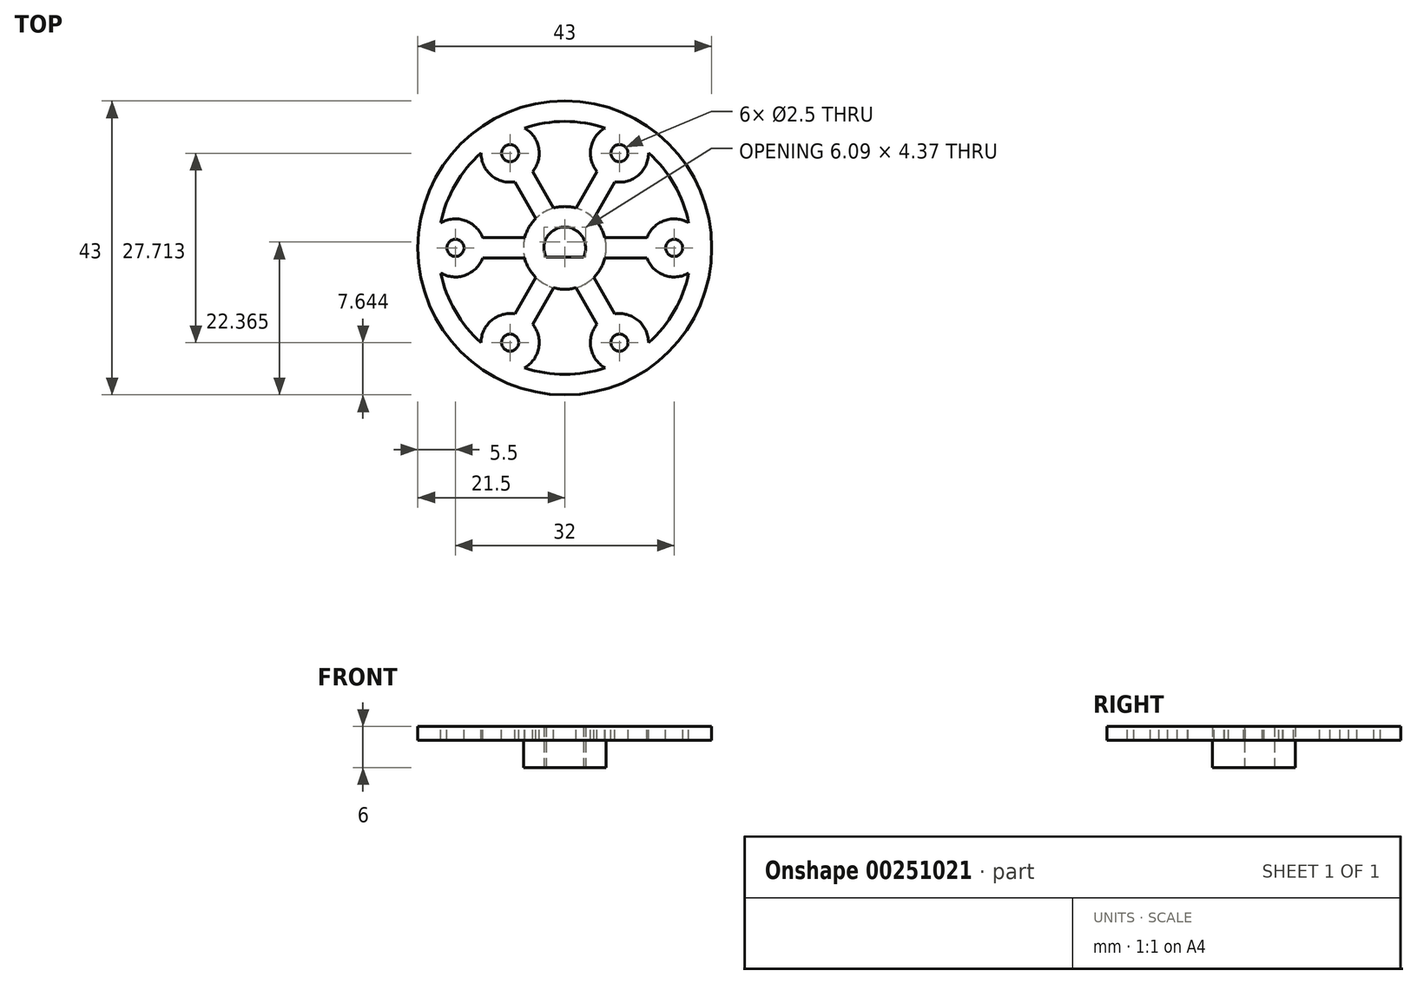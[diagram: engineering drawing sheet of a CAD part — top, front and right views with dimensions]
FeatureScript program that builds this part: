
annotation { "Feature Type Name" : "Feature", "Feature Type Description" : "" }
export const myFeature = defineFeature(function(context is Context, id is Id, definition is map)
    precondition{}
    {
        {
            var Q0;
            Q0=qCreatedBy(makeId("Top.planeOp"),FACE);
            var sketch = newSketch(context, id + "F0", { "sketchPlane" : qUnion([Q0])});
            skCircle(sketch, "E0", {"center": v(0, 0) * mm, "radius": 3.05 * mm, "construction": true});
            skLineSegment(sketch, "E1", {"start": v(-2.75, -1.32) * mm, "end": v(2.75, -1.32) * mm});
            skArc(sketch, "E2", {"start": v(2.75, -1.32) * mm, "mid": v(0, 3.05) * mm, "end": v(-2.75, -1.32) * mm});
            skCircle(sketch, "E3", {"center": v(0, 0) * mm, "radius": 6.05 * mm});
            skSolve(sketch);
        }
        {
            var Q0;
            Q0 = qSketchRegion(id + "F0", true);
            extrude(context, id + "F1", {"entities" : qUnion([Q0]), "depth" : 6 * mm});
        }
        {
            var Q0;
            Q0=makeQuery(id+"F1.opExtrude","CAP_FACE",FACE,{"disambiguationData":[OSD([sQuery(id+"F0.wireOp",EDGE,"E1"),sQuery(id+"F0.wireOp",EDGE,"E2"),sQuery(id+"F0.wireOp",EDGE,"E3")])],"isStart":false});
            var sketch = newSketch(context, id + "F2", { "sketchPlane" : qUnion([Q0])});
            skCircle(sketch, "E4", {"center": v(0, 0) * mm, "radius": 21.5 * mm});
            skCircle(sketch, "E5", {"center": v(0, 0) * mm, "radius": 18.5 * mm});
            skCircle(sketch, "E6", {"center": v(-16, 0) * mm, "radius": 1.25 * mm});
            skCircle(sketch, "E7", {"center": v(-16, 0) * mm, "radius": 4.25 * mm});
            skCircle(sketch, "E8.1.0", {"center": v(-8, -13.86) * mm, "radius": 1.25 * mm});
            skCircle(sketch, "E8.1.1", {"center": v(-8, -13.86) * mm, "radius": 4.25 * mm});
            skCircle(sketch, "E8.2.0", {"center": v(8, -13.86) * mm, "radius": 1.25 * mm});
            skCircle(sketch, "E8.2.1", {"center": v(8, -13.86) * mm, "radius": 4.25 * mm});
            skCircle(sketch, "E8.3.0", {"center": v(16, 0) * mm, "radius": 1.25 * mm});
            skCircle(sketch, "E8.3.1", {"center": v(16, 0) * mm, "radius": 4.25 * mm});
            skCircle(sketch, "E8.4.0", {"center": v(8, 13.86) * mm, "radius": 1.25 * mm});
            skCircle(sketch, "E8.4.1", {"center": v(8, 13.86) * mm, "radius": 4.25 * mm});
            skCircle(sketch, "E8.5.0", {"center": v(-8, 13.86) * mm, "radius": 1.25 * mm});
            skCircle(sketch, "E8.5.1", {"center": v(-8, 13.86) * mm, "radius": 4.25 * mm});
            skLineSegment(sketch, "E9.bottom", {"start": v(-4, 1.5) * mm, "end": v(-14, 1.5) * mm});
            skLineSegment(sketch, "E9.top", {"start": v(-4, -1.5) * mm, "end": v(-14, -1.5) * mm});
            skLineSegment(sketch, "E9.left", {"start": v(-4, 1.5) * mm, "end": v(-4, -1.5) * mm});
            skLineSegment(sketch, "E9.right", {"start": v(-14, 1.5) * mm, "end": v(-14, -1.5) * mm});
            skPoint(sketch, "E9.middle", {"position": v(-9, 0) * mm});
            skLineSegment(sketch, "E10.1.0", {"start": v(-3.3, -2.71) * mm, "end": v(-8.3, -11.37) * mm});
            skLineSegment(sketch, "E10.1.1", {"start": v(-8.3, -11.37) * mm, "end": v(-5.7, -12.87) * mm});
            skLineSegment(sketch, "E10.1.2", {"start": v(-0.7, -4.21) * mm, "end": v(-5.7, -12.87) * mm});
            skLineSegment(sketch, "E10.1.3", {"start": v(-3.3, -2.71) * mm, "end": v(-0.7, -4.21) * mm});
            skLineSegment(sketch, "E10.2.0", {"start": v(0.7, -4.21) * mm, "end": v(5.7, -12.87) * mm});
            skLineSegment(sketch, "E10.2.1", {"start": v(5.7, -12.87) * mm, "end": v(8.3, -11.37) * mm});
            skLineSegment(sketch, "E10.2.2", {"start": v(3.3, -2.71) * mm, "end": v(8.3, -11.37) * mm});
            skLineSegment(sketch, "E10.2.3", {"start": v(0.7, -4.21) * mm, "end": v(3.3, -2.71) * mm});
            skLineSegment(sketch, "E10.3.0", {"start": v(4, -1.5) * mm, "end": v(14, -1.5) * mm});
            skLineSegment(sketch, "E10.3.1", {"start": v(14, -1.5) * mm, "end": v(14, 1.5) * mm});
            skLineSegment(sketch, "E10.3.2", {"start": v(4, 1.5) * mm, "end": v(14, 1.5) * mm});
            skLineSegment(sketch, "E10.3.3", {"start": v(4, -1.5) * mm, "end": v(4, 1.5) * mm});
            skLineSegment(sketch, "E10.4.0", {"start": v(3.3, 2.71) * mm, "end": v(8.3, 11.37) * mm});
            skLineSegment(sketch, "E10.4.1", {"start": v(8.3, 11.37) * mm, "end": v(5.7, 12.87) * mm});
            skLineSegment(sketch, "E10.4.2", {"start": v(0.7, 4.21) * mm, "end": v(5.7, 12.87) * mm});
            skLineSegment(sketch, "E10.4.3", {"start": v(3.3, 2.71) * mm, "end": v(0.7, 4.21) * mm});
            skLineSegment(sketch, "E10.5.0", {"start": v(-0.7, 4.21) * mm, "end": v(-5.7, 12.87) * mm});
            skLineSegment(sketch, "E10.5.1", {"start": v(-5.7, 12.87) * mm, "end": v(-8.3, 11.37) * mm});
            skLineSegment(sketch, "E10.5.2", {"start": v(-3.3, 2.71) * mm, "end": v(-8.3, 11.37) * mm});
            skLineSegment(sketch, "E10.5.3", {"start": v(-0.7, 4.21) * mm, "end": v(-3.3, 2.71) * mm});
            skSolve(sketch);
        }
        {
            var Q0;
            Q0 = qSketchRegion(id + "F2", true);
            var Q1;
            Q1=makeQuery(id+"F2.imprint","IMPRINT",FACE,{"disambiguationData":[TD([[makeQuery(id+"F2.imprint","IMPRINT",EDGE,{"derivedFrom":sQuery(id+"F2.wireOp",EDGE,"E6")}),-1.0]])]});
            var Q2;
            Q2=makeQuery(id+"F2.imprint","IMPRINT",FACE,{"disambiguationData":[TD([[makeQuery(id+"F2.imprint","IMPRINT",EDGE,{"derivedFrom":sQuery(id+"F2.wireOp",EDGE,"E8.5.0")}),-1.0]])]});
            var Q3;
            Q3=makeQuery(id+"F2.imprint","IMPRINT",FACE,{"disambiguationData":[TD([[makeQuery(id+"F2.imprint","IMPRINT",EDGE,{"derivedFrom":sQuery(id+"F2.wireOp",EDGE,"E8.4.0")}),-1.0]])]});
            var Q4;
            Q4=makeQuery(id+"F2.imprint","IMPRINT",FACE,{"disambiguationData":[TD([[makeQuery(id+"F2.imprint","IMPRINT",EDGE,{"derivedFrom":sQuery(id+"F2.wireOp",EDGE,"E8.3.0")}),-1.0]])]});
            var Q5;
            Q5=makeQuery(id+"F2.imprint","IMPRINT",FACE,{"disambiguationData":[TD([[makeQuery(id+"F2.imprint","IMPRINT",EDGE,{"derivedFrom":sQuery(id+"F2.wireOp",EDGE,"E8.2.0")}),-1.0]])]});
            var Q6;
            Q6=makeQuery(id+"F2.imprint","IMPRINT",FACE,{"disambiguationData":[TD([[makeQuery(id+"F2.imprint","IMPRINT",EDGE,{"derivedFrom":sQuery(id+"F2.wireOp",EDGE,"E8.1.0")}),-1.0]])]});
            var Q7;
            {var subQ0=sQuery(id+"F2.wireOp",EDGE,"E8.5.1");var subQ1=sQuery(id+"F2.wireOp",EDGE,"E5");var subQ2=makeQuery(id+"F2.imprint","INTERSECT",VERTEX,{"disambiguationData":[OD(0.0)],"derivedFrom":[subQ1,subQ0]});Q7=makeQuery(id+"F2.imprint","IMPRINT",FACE,{"disambiguationData":[TD([[makeQuery(id+"F2.imprint","IMPRINT",EDGE,{"disambiguationData":[TD([[subQ2,-1.0]])],"derivedFrom":subQ1}),-1.0]])]});}
            var Q8;
            {var subQ0=sQuery(id+"F2.wireOp",EDGE,"E7");var subQ1=sQuery(id+"F2.wireOp",EDGE,"E5");var subQ2=makeQuery(id+"F2.imprint","INTERSECT",VERTEX,{"disambiguationData":[OD(0.0)],"derivedFrom":[subQ1,subQ0]});Q8=makeQuery(id+"F2.imprint","IMPRINT",FACE,{"disambiguationData":[TD([[makeQuery(id+"F2.imprint","IMPRINT",EDGE,{"disambiguationData":[TD([[subQ2,-1.0]])],"derivedFrom":subQ1}),-1.0]])]});}
            var Q9;
            {var subQ0=sQuery(id+"F2.wireOp",EDGE,"E8.1.1");var subQ1=sQuery(id+"F2.wireOp",EDGE,"E5");var subQ2=makeQuery(id+"F2.imprint","INTERSECT",VERTEX,{"disambiguationData":[OD(0.0)],"derivedFrom":[subQ1,subQ0]});Q9=makeQuery(id+"F2.imprint","IMPRINT",FACE,{"disambiguationData":[TD([[makeQuery(id+"F2.imprint","IMPRINT",EDGE,{"disambiguationData":[TD([[subQ2,-1.0]])],"derivedFrom":subQ1}),-1.0]])]});}
            var Q10;
            {var subQ0=sQuery(id+"F2.wireOp",EDGE,"E8.2.1");var subQ1=sQuery(id+"F2.wireOp",EDGE,"E5");var subQ2=makeQuery(id+"F2.imprint","INTERSECT",VERTEX,{"disambiguationData":[OD(0.0)],"derivedFrom":[subQ1,subQ0]});Q10=makeQuery(id+"F2.imprint","IMPRINT",FACE,{"disambiguationData":[TD([[makeQuery(id+"F2.imprint","IMPRINT",EDGE,{"disambiguationData":[TD([[subQ2,-1.0]])],"derivedFrom":subQ1}),-1.0]])]});}
            var Q11;
            {var subQ0=sQuery(id+"F2.wireOp",EDGE,"E8.3.1");var subQ1=sQuery(id+"F2.wireOp",EDGE,"E5");var subQ2=makeQuery(id+"F2.imprint","INTERSECT",VERTEX,{"disambiguationData":[OD(0.0)],"derivedFrom":[subQ1,subQ0]});Q11=makeQuery(id+"F2.imprint","IMPRINT",FACE,{"disambiguationData":[TD([[makeQuery(id+"F2.imprint","IMPRINT",EDGE,{"disambiguationData":[TD([[subQ2,1.0]])],"derivedFrom":subQ1}),-1.0]])]});}
            var Q12;
            {var subQ0=sQuery(id+"F2.wireOp",EDGE,"E8.4.1");var subQ1=sQuery(id+"F2.wireOp",EDGE,"E5");var subQ2=makeQuery(id+"F2.imprint","INTERSECT",VERTEX,{"disambiguationData":[OD(0.0)],"derivedFrom":[subQ1,subQ0]});Q12=makeQuery(id+"F2.imprint","IMPRINT",FACE,{"disambiguationData":[TD([[makeQuery(id+"F2.imprint","IMPRINT",EDGE,{"disambiguationData":[TD([[subQ2,-1.0]])],"derivedFrom":subQ1}),-1.0]])]});}
            var Q13;
            {var subQ0=sQuery(id+"F2.wireOp",EDGE,"E10.5.0");var subQ1=sQuery(id+"F2.wireOp",EDGE,"E8.5.1");var subQ2=makeQuery(id+"F2.imprint","INTERSECT",VERTEX,{"derivedFrom":[subQ1,subQ0]});Q13=makeQuery(id+"F2.imprint","IMPRINT",FACE,{"disambiguationData":[TD([[makeQuery(id+"F2.imprint","IMPRINT",EDGE,{"disambiguationData":[TD([[subQ2,1.0]])],"derivedFrom":subQ1}),-1.0]])]});}
            var Q14;
            {var subQ5=sQuery(id+"F2.wireOp",EDGE,"E10.5.1");Q14=makeQuery(id+"F2.imprint","IMPRINT",FACE,{"disambiguationData":[TD([[makeQuery(id+"F2.imprint","IMPRINT",EDGE,{"derivedFrom":subQ5}),1.0]])]});}
            var Q15;
            {var subQ5=sQuery(id+"F2.wireOp",EDGE,"E10.4.1");Q15=makeQuery(id+"F2.imprint","IMPRINT",FACE,{"disambiguationData":[TD([[makeQuery(id+"F2.imprint","IMPRINT",EDGE,{"derivedFrom":subQ5}),1.0]])]});}
            var Q16;
            {var subQ0=sQuery(id+"F2.wireOp",EDGE,"E10.4.0");var subQ1=sQuery(id+"F2.wireOp",EDGE,"E8.4.1");var subQ2=makeQuery(id+"F2.imprint","INTERSECT",VERTEX,{"derivedFrom":[subQ1,subQ0]});Q16=makeQuery(id+"F2.imprint","IMPRINT",FACE,{"disambiguationData":[TD([[makeQuery(id+"F2.imprint","IMPRINT",EDGE,{"disambiguationData":[TD([[subQ2,1.0]])],"derivedFrom":subQ1}),-1.0]])]});}
            var Q17;
            {var subQ0=sQuery(id+"F2.wireOp",EDGE,"E10.3.0");var subQ1=sQuery(id+"F2.wireOp",EDGE,"E8.3.1");var subQ2=makeQuery(id+"F2.imprint","INTERSECT",VERTEX,{"derivedFrom":[subQ1,subQ0]});Q17=makeQuery(id+"F2.imprint","IMPRINT",FACE,{"disambiguationData":[TD([[makeQuery(id+"F2.imprint","IMPRINT",EDGE,{"disambiguationData":[TD([[subQ2,1.0]])],"derivedFrom":subQ1}),-1.0]])]});}
            var Q18;
            {var subQ5=sQuery(id+"F2.wireOp",EDGE,"E10.3.1");Q18=makeQuery(id+"F2.imprint","IMPRINT",FACE,{"disambiguationData":[TD([[makeQuery(id+"F2.imprint","IMPRINT",EDGE,{"derivedFrom":subQ5}),1.0]])]});}
            var Q19;
            {var subQ0=sQuery(id+"F2.wireOp",EDGE,"E10.2.0");var subQ1=sQuery(id+"F2.wireOp",EDGE,"E8.2.1");var subQ2=makeQuery(id+"F2.imprint","INTERSECT",VERTEX,{"derivedFrom":[subQ1,subQ0]});Q19=makeQuery(id+"F2.imprint","IMPRINT",FACE,{"disambiguationData":[TD([[makeQuery(id+"F2.imprint","IMPRINT",EDGE,{"disambiguationData":[TD([[subQ2,1.0]])],"derivedFrom":subQ1}),-1.0]])]});}
            var Q20;
            {var subQ5=sQuery(id+"F2.wireOp",EDGE,"E10.2.1");Q20=makeQuery(id+"F2.imprint","IMPRINT",FACE,{"disambiguationData":[TD([[makeQuery(id+"F2.imprint","IMPRINT",EDGE,{"derivedFrom":subQ5}),1.0]])]});}
            var Q21;
            {var subQ0=sQuery(id+"F2.wireOp",EDGE,"E10.1.0");var subQ1=sQuery(id+"F2.wireOp",EDGE,"E8.1.1");var subQ2=makeQuery(id+"F2.imprint","INTERSECT",VERTEX,{"derivedFrom":[subQ1,subQ0]});Q21=makeQuery(id+"F2.imprint","IMPRINT",FACE,{"disambiguationData":[TD([[makeQuery(id+"F2.imprint","IMPRINT",EDGE,{"disambiguationData":[TD([[subQ2,1.0]])],"derivedFrom":subQ1}),-1.0]])]});}
            var Q22;
            {var subQ5=sQuery(id+"F2.wireOp",EDGE,"E10.1.1");Q22=makeQuery(id+"F2.imprint","IMPRINT",FACE,{"disambiguationData":[TD([[makeQuery(id+"F2.imprint","IMPRINT",EDGE,{"derivedFrom":subQ5}),1.0]])]});}
            var Q23;
            {var subQ0=sQuery(id+"F2.wireOp",EDGE,"E9.bottom");var subQ1=sQuery(id+"F2.wireOp",EDGE,"E7");var subQ2=makeQuery(id+"F2.imprint","INTERSECT",VERTEX,{"derivedFrom":[subQ1,subQ0]});Q23=makeQuery(id+"F2.imprint","IMPRINT",FACE,{"disambiguationData":[TD([[makeQuery(id+"F2.imprint","IMPRINT",EDGE,{"disambiguationData":[TD([[subQ2,1.0]])],"derivedFrom":subQ1}),-1.0]])]});}
            var Q24;
            {var subQ5=sQuery(id+"F2.wireOp",EDGE,"E9.right");Q24=makeQuery(id+"F2.imprint","IMPRINT",FACE,{"disambiguationData":[TD([[makeQuery(id+"F2.imprint","IMPRINT",EDGE,{"derivedFrom":subQ5}),1.0]])]});}
            extrude(context, id + "F3", {"entities" : qUnion([Q0, Q1, Q2, Q3, Q4, Q5, Q6, Q7, Q8, Q9, Q10, Q11, Q12, Q13, Q14, Q15, Q16, Q17, Q18, Q19, Q20, Q21, Q22, Q23, Q24]), "operationType" : NewBodyOperationType.ADD, "oppositeDirection" : true, "depth" : 2 * mm});
        }
    });
